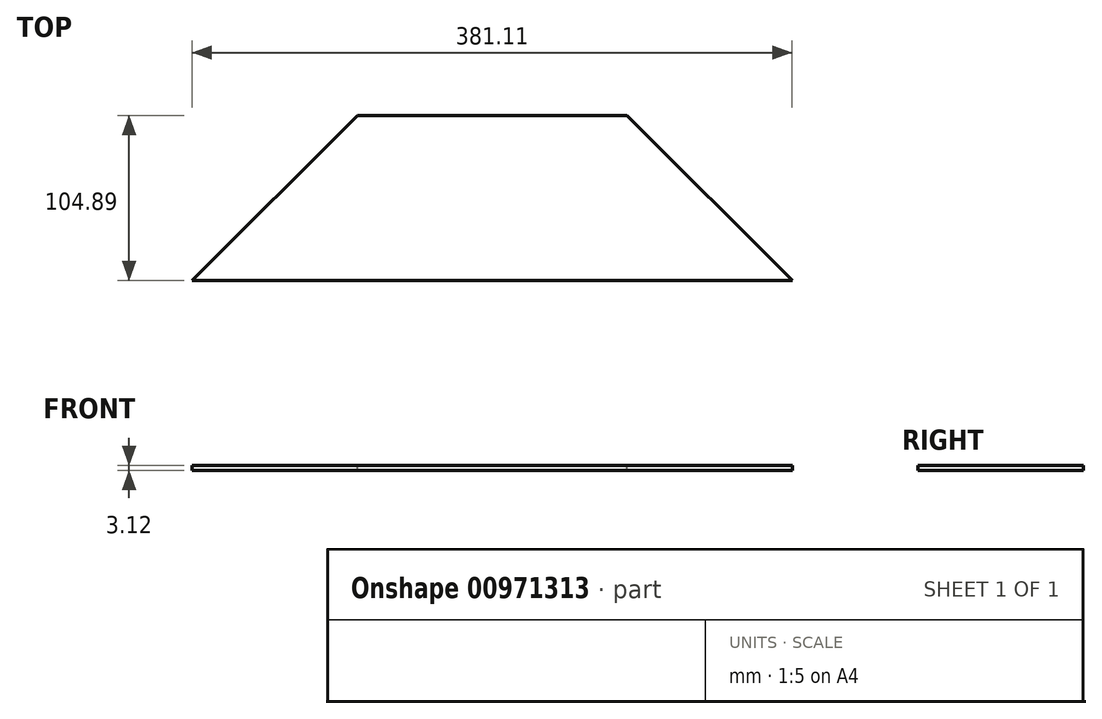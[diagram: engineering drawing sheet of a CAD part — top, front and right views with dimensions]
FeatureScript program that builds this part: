
annotation { "Feature Type Name" : "Feature", "Feature Type Description" : "" }
export const myFeature = defineFeature(function(context is Context, id is Id, definition is map)
    precondition{}
    {
        {
            var Q0;
            Q0=qCreatedBy(makeId("Top.planeOp"),FACE);
            var sketch = newSketch(context, id + "F0", { "sketchPlane" : qUnion([Q0])});
            skLineSegment(sketch, "E0.bottom", {"start": v(-277.77, 191.7) * mm, "end": v(319.13, 191.7) * mm});
            skLineSegment(sketch, "E0.top", {"start": v(-277.77, -144.85) * mm, "end": v(319.13, -144.85) * mm});
            skLineSegment(sketch, "E0.left", {"start": v(-277.77, 191.7) * mm, "end": v(-277.77, -144.85) * mm});
            skLineSegment(sketch, "E0.right", {"start": v(319.13, 191.7) * mm, "end": v(319.13, -144.85) * mm});
            skSolve(sketch);
        }
        {
            var Q0;
            Q0=makeQuery(id+"F0.imprint","IMPRINT",FACE,{"disambiguationData":[TD([[makeQuery(id+"F0.imprint","IMPRINT",EDGE,{"derivedFrom":sQuery(id+"F0.wireOp",EDGE,"E0.bottom")}),-1.0]])]});
            var sketch = newSketch(context, id + "F1", { "sketchPlane" : qUnion([Q0])});
            skLineSegment(sketch, "E1", {"start": v(-118.09, -144.85) * mm, "end": v(-13.2, -39.96) * mm});
            skLineSegment(sketch, "E2", {"start": v(-13.2, -39.96) * mm, "end": v(158.13, -39.96) * mm});
            skLineSegment(sketch, "E3", {"start": v(158.13, -39.96) * mm, "end": v(263.02, -144.85) * mm});
            skLineSegment(sketch, "E4", {"start": v(-118.09, -144.85) * mm, "end": v(263.02, -144.85) * mm});
            skSolve(sketch);
        }
        {
            var Q0;
            Q0=sQuery(id+"F1.wireOp",EDGE,"E1");
            var Q1;
            Q1=sQuery(id+"F1.wireOp",EDGE,"E2");
            var Q2;
            Q2=sQuery(id+"F1.wireOp",EDGE,"E3");
            var Q3;
            Q3=sQuery(id+"F1.wireOp",EDGE,"E4");
            extrude(context, id + "F2", {"bodyType" : ToolBodyType.SURFACE, "surfaceEntities" : qUnion([Q0, Q1, Q2, Q3]), "depth" : 3.12 * mm, "offsetDistance" : 25.4 * mm});
        }
    });
